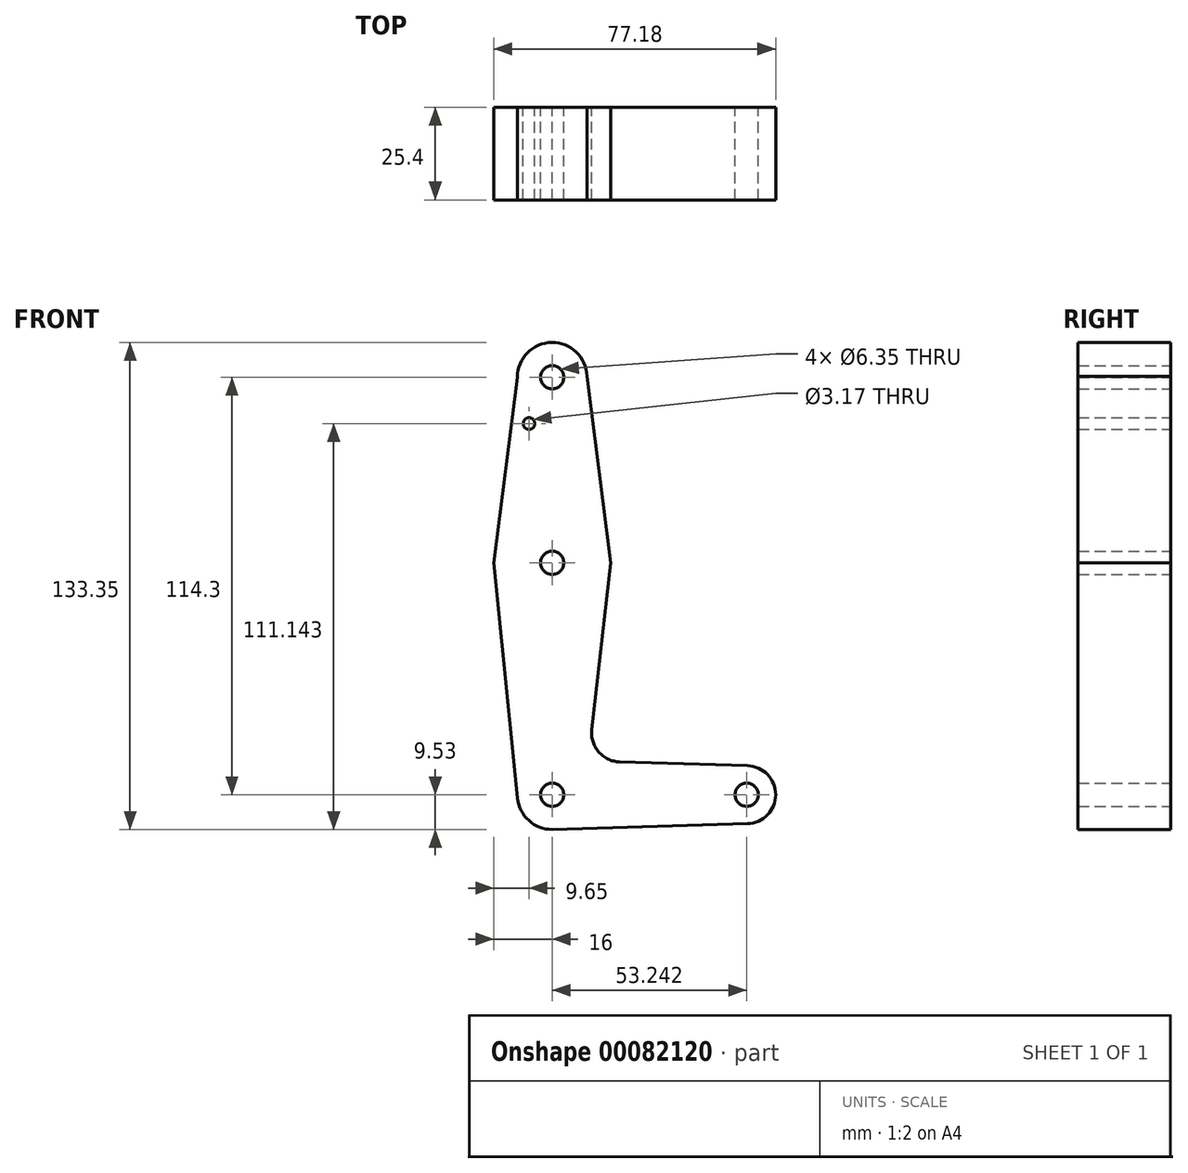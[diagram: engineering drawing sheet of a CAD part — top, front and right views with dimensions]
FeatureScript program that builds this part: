
annotation { "Feature Type Name" : "Feature", "Feature Type Description" : "" }
export const myFeature = defineFeature(function(context is Context, id is Id, definition is map)
    precondition{}
    {
        {
            var Q0;
            Q0=qCreatedBy(makeId("Front.planeOp"),FACE);
            var sketch = newSketch(context, id + "F0", { "sketchPlane" : qUnion([Q0])});
            skLineSegment(sketch, "E0", {"start": v(0, 50.8) * mm, "end": v(0, 0) * mm});
            skLineSegment(sketch, "E1", {"start": v(0, 0) * mm, "end": v(0, -63.5) * mm});
            skLineSegment(sketch, "E2", {"start": v(0, -63.5) * mm, "end": v(8.8, -63.5) * mm});
            skLineSegment(sketch, "E3", {"start": v(8.8, -63.5) * mm, "end": v(53.24, -63.5) * mm});
            skCircle(sketch, "E4", {"center": v(0, 50.8) * mm, "radius": 9.52 * mm});
            skCircle(sketch, "E5", {"center": v(0, 0) * mm, "radius": 15.88 * mm});
            skCircle(sketch, "E6", {"center": v(0, -63.5) * mm, "radius": 9.53 * mm});
            skCircle(sketch, "E7", {"center": v(53.24, -63.5) * mm, "radius": 7.94 * mm});
            skLineSegment(sketch, "E8", {"start": v(0, 50.8) * mm, "end": v(0, -63.5) * mm});
            skLineSegment(sketch, "E9", {"start": v(-9.52, 50.83) * mm, "end": v(-16, 0) * mm});
            skLineSegment(sketch, "E10", {"start": v(-16, 0) * mm, "end": v(-9.48, -64.46) * mm});
            skLineSegment(sketch, "E11", {"start": v(9.52, 51.08) * mm, "end": v(16, 0) * mm});
            skLineSegment(sketch, "E12", {"start": v(16, 0) * mm, "end": v(10.81, -45.68) * mm});
            skLineSegment(sketch, "E13", {"start": v(0, -73.03) * mm, "end": v(53.48, -71.43) * mm});
            skLineSegment(sketch, "E14", {"start": v(18.48, -54.52) * mm, "end": v(53.48, -55.57) * mm});
            skCircle(sketch, "E15", {"center": v(0, 50.8) * mm, "radius": 3.18 * mm});
            skCircle(sketch, "E16", {"center": v(-6.35, 38.11) * mm, "radius": 1.59 * mm});
            skCircle(sketch, "E17", {"center": v(0, 0) * mm, "radius": 3.18 * mm});
            skCircle(sketch, "E18", {"center": v(0, -63.5) * mm, "radius": 3.18 * mm});
            skCircle(sketch, "E19", {"center": v(53.24, -63.5) * mm, "radius": 3.18 * mm});
            skArc(sketch, "E20.filletArc", {"start": v(10.81, -45.68) * mm, "mid": v(12.7, -51.78) * mm, "end": v(18.48, -54.52) * mm});
            skSolve(sketch);
        }
        {
            var Q0;
            Q0=makeQuery(id+"F0.imprint","IMPRINT",FACE,{"disambiguationData":[TD([[makeQuery(id+"F0.imprint","IMPRINT",EDGE,{"derivedFrom":sQuery(id+"F0.wireOp",EDGE,"E15")}),-1.0]])]});
            var Q1;
            {var subQ0=sQuery(id+"F0.wireOp",EDGE,"E11");var subQ1=sQuery(id+"F0.wireOp",EDGE,"E4");var subQ2=makeQuery(id+"F0.imprint","INTERSECT",VERTEX,{"derivedFrom":[subQ1,subQ0]});Q1=makeQuery(id+"F0.imprint","IMPRINT",FACE,{"disambiguationData":[TD([[makeQuery(id+"F0.imprint","IMPRINT",EDGE,{"disambiguationData":[TD([[subQ2,1.0]])],"derivedFrom":subQ1}),-1.0]])]});}
            var Q2;
            Q2=makeQuery(id+"F0.imprint","IMPRINT",FACE,{"disambiguationData":[TD([[makeQuery(id+"F0.imprint","IMPRINT",EDGE,{"derivedFrom":sQuery(id+"F0.wireOp",EDGE,"E16")}),-1.0]])]});
            var Q3;
            {var subQ1=sQuery(id+"F0.wireOp",EDGE,"E5");var subQ5=makeQuery(id+"F0.imprint","INTERSECT",VERTEX,{"derivedFrom":[subQ1,sQuery(id+"F0.wireOp",EDGE,"E11")]});Q3=makeQuery(id+"F0.imprint","IMPRINT",FACE,{"disambiguationData":[TD([[makeQuery(id+"F0.imprint","IMPRINT",EDGE,{"disambiguationData":[TD([[subQ5,-1.0]])],"derivedFrom":subQ1}),1.0]])]});}
            var Q4;
            {var subQ1=sQuery(id+"F0.wireOp",EDGE,"E5");var subQ5=makeQuery(id+"F0.imprint","INTERSECT",VERTEX,{"derivedFrom":[subQ1,sQuery(id+"F0.wireOp",EDGE,"E9")]});Q4=makeQuery(id+"F0.imprint","IMPRINT",FACE,{"disambiguationData":[TD([[makeQuery(id+"F0.imprint","IMPRINT",EDGE,{"disambiguationData":[TD([[subQ5,1.0]])],"derivedFrom":subQ1}),1.0]])]});}
            var Q5;
            {var subQ0=sQuery(id+"F0.wireOp",EDGE,"E10");Q5=makeQuery(id+"F0.imprint","IMPRINT",FACE,{"disambiguationData":[TD([[makeQuery(id+"F0.imprint","IMPRINT",EDGE,{"derivedFrom":subQ0}),1.0]])]});}
            var Q6;
            {var subQ12=sQuery(id+"F0.wireOp",EDGE,"E12");Q6=makeQuery(id+"F0.imprint","IMPRINT",FACE,{"disambiguationData":[TD([[makeQuery(id+"F0.imprint","IMPRINT",EDGE,{"derivedFrom":subQ12}),-1.0]])]});}
            var Q7;
            {var subQ5=sQuery(id+"F0.wireOp",EDGE,"E3");var subQ7=sQuery(id+"F0.wireOp",EDGE,"E2");var subQ8=makeQuery(id+"F0.imprint","INTERSECT",VERTEX,{"derivedFrom":[subQ7,subQ5]});Q7=makeQuery(id+"F0.imprint","IMPRINT",FACE,{"disambiguationData":[TD([[makeQuery(id+"F0.imprint","IMPRINT",EDGE,{"disambiguationData":[TD([[subQ8,1.0]])],"derivedFrom":subQ7}),1.0]])]});}
            var Q8;
            {var subQ6=sQuery(id+"F0.wireOp",EDGE,"E3");var subQ7=sQuery(id+"F0.wireOp",EDGE,"E2");var subQ8=makeQuery(id+"F0.imprint","INTERSECT",VERTEX,{"derivedFrom":[subQ7,subQ6]});Q8=makeQuery(id+"F0.imprint","IMPRINT",FACE,{"disambiguationData":[TD([[makeQuery(id+"F0.imprint","IMPRINT",EDGE,{"disambiguationData":[TD([[subQ8,1.0]])],"derivedFrom":subQ7}),-1.0]])]});}
            var Q9;
            {var subQ0=sQuery(id+"F0.wireOp",EDGE,"E7");var subQ1=sQuery(id+"F0.wireOp",EDGE,"E3");var subQ2=makeQuery(id+"F0.imprint","INTERSECT",VERTEX,{"derivedFrom":[subQ1,subQ0]});Q9=makeQuery(id+"F0.imprint","IMPRINT",FACE,{"disambiguationData":[TD([[makeQuery(id+"F0.imprint","IMPRINT",EDGE,{"disambiguationData":[TD([[subQ2,1.0]])],"derivedFrom":subQ1}),-1.0]])]});}
            var Q10;
            Q10=makeQuery(id+"F0.imprint","IMPRINT",FACE,{"disambiguationData":[TD([[makeQuery(id+"F0.imprint","IMPRINT",EDGE,{"derivedFrom":sQuery(id+"F0.wireOp",EDGE,"E19")}),-1.0]])]});
            extrude(context, id + "F1", {"entities" : qUnion([Q0, Q1, Q2, Q3, Q4, Q5, Q6, Q7, Q8, Q9, Q10]), "depth" : 25.4 * mm});
        }
    });
